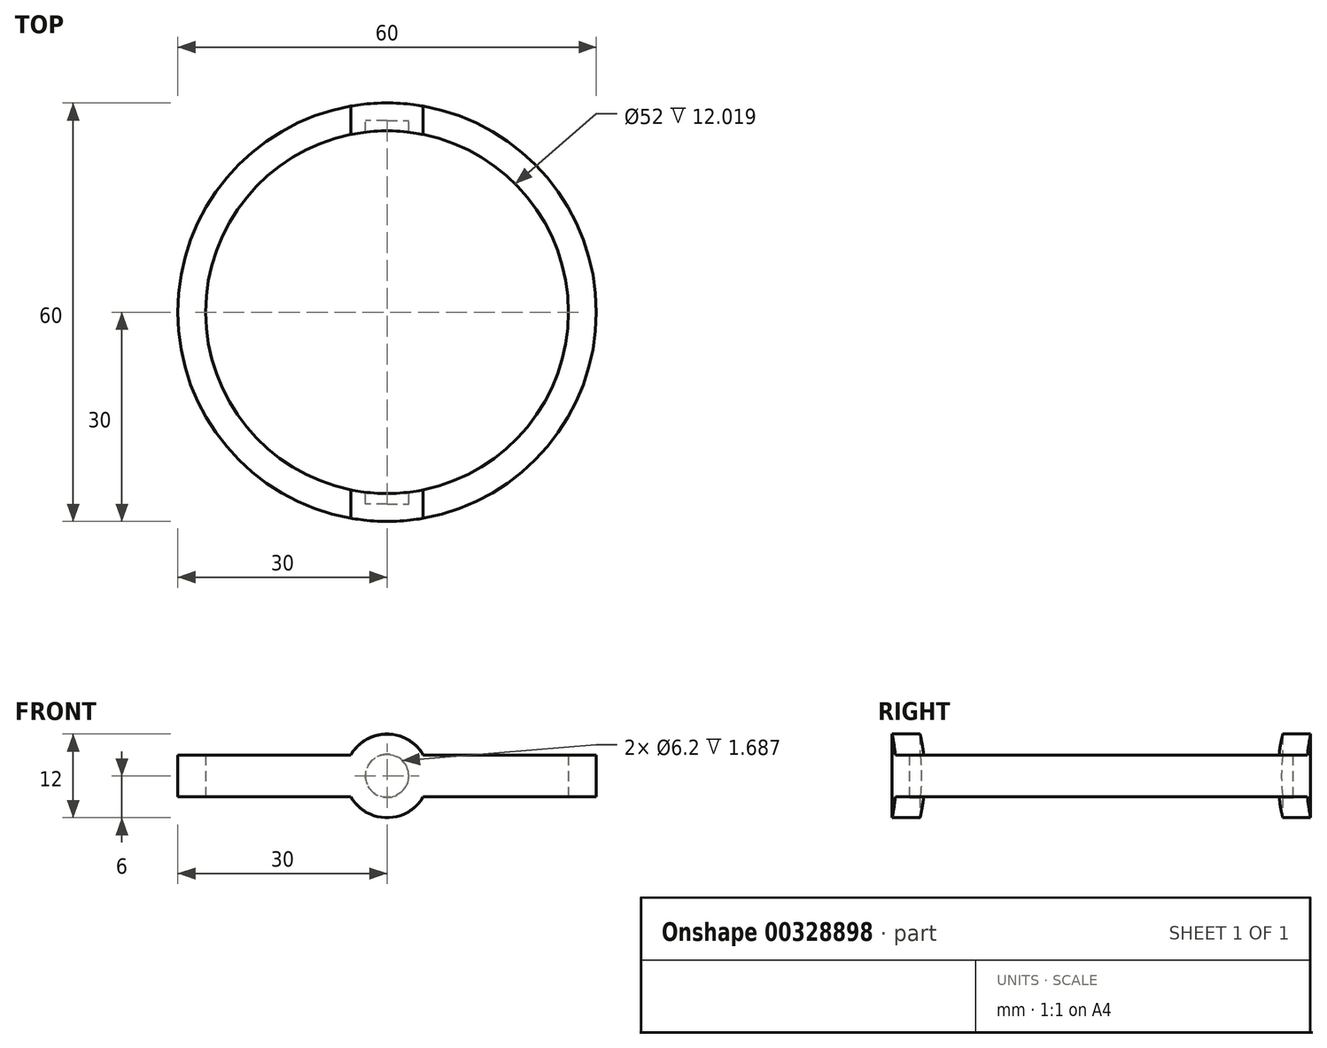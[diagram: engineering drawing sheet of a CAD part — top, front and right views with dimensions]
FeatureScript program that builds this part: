
annotation { "Feature Type Name" : "Feature", "Feature Type Description" : "" }
export const myFeature = defineFeature(function(context is Context, id is Id, definition is map)
    precondition{}
    {
        {
            var Q0;
            Q0=qCreatedBy(makeId("Front.planeOp"),FACE);
            var sketch = newSketch(context, id + "F0", { "sketchPlane" : qUnion([Q0])});
            skCircle(sketch, "E0", {"center": v(0, 0) * mm, "radius": 3 * mm, "construction": true});
            skCircle(sketch, "E1", {"center": v(0, 0) * mm, "radius": 1.5 * mm, "construction": true});
            skCircle(sketch, "E2", {"center": v(0, 0) * mm, "radius": 6 * mm});
            skLineSegment(sketch, "E3", {"start": v(2.65, 1.4) * mm, "end": v(5.3, 2.8) * mm, "construction": true});
            skLineSegment(sketch, "E4.bottom", {"start": v(0, -3) * mm, "end": v(-26, -3) * mm, "construction": true});
            skLineSegment(sketch, "E4.top", {"start": v(0, 3) * mm, "end": v(-26, 3) * mm, "construction": true});
            skLineSegment(sketch, "E4.left", {"start": v(0, -3) * mm, "end": v(0, 3) * mm});
            skLineSegment(sketch, "E4.right", {"start": v(-30, -3) * mm, "end": v(-30, 3) * mm});
            skLineSegment(sketch, "E5", {"start": v(-26, 3) * mm, "end": v(-26, -3) * mm});
            skLineSegment(sketch, "E6", {"start": v(-26, 3) * mm, "end": v(-26, 6) * mm});
            skLineSegment(sketch, "E7", {"start": v(-26, 6) * mm, "end": v(0, 6) * mm});
            skLineSegment(sketch, "E8", {"start": v(-26, -3) * mm, "end": v(-26, -6) * mm});
            skLineSegment(sketch, "E9", {"start": v(-26, -6) * mm, "end": v(0, -6) * mm});
            skLineSegment(sketch, "E10", {"start": v(0, 3) * mm, "end": v(0, 6) * mm});
            skLineSegment(sketch, "E11", {"start": v(0, -3) * mm, "end": v(0, -6) * mm});
            skLineSegment(sketch, "E12", {"start": v(-26, 3) * mm, "end": v(-30, 3) * mm});
            skLineSegment(sketch, "E13", {"start": v(-26, -3) * mm, "end": v(-30, -3) * mm});
            skSolve(sketch);
        }
        {
            var Q0;
            Q0=qCreatedBy(makeId("Front.planeOp"),FACE);
            var sketch = newSketch(context, id + "F1", { "sketchPlane" : qUnion([Q0])});
            skCircle(sketch, "E14.0", {"center": v(0, 0) * mm, "radius": 3 * mm, "construction": true});
            skCircle(sketch, "E15.0", {"center": v(0, 0) * mm, "radius": 1.5 * mm, "construction": true});
            skCircle(sketch, "E16.0", {"center": v(0, 0) * mm, "radius": 3.1 * mm});
            skCircle(sketch, "E17.0", {"center": v(0, 0) * mm, "radius": 1.55 * mm});
            skSolve(sketch);
        }
        {
            var Q0;
            {var subQ0=sQuery(id+"F0.wireOp",EDGE,"E4.right");Q0=makeQuery(id+"F0.imprint","IMPRINT",FACE,{"disambiguationData":[TD([[makeQuery(id+"F0.imprint","IMPRINT",EDGE,{"derivedFrom":subQ0}),-1.0]])]});}
            var Q1;
            Q1=sQuery(id+"F0.wireOp",EDGE,"E4.left");
            revolve(context, id + "F2", {"entities" : qUnion([Q0]), "axis" : qUnion([Q1]), "revolveType" : RevolveType.FULL});
        }
        {
            var Q0;
            Q0=makeQuery(id+"F0.imprint","IMPRINT",FACE,{"disambiguationData":[TD([[makeQuery(id+"F0.imprint","IMPRINT",EDGE,{"derivedFrom":sQuery(id+"F0.wireOp",EDGE,"E4.left")}),1.0]])]});
            var Q1;
            Q1=makeQuery(id+"F0.imprint","IMPRINT",FACE,{"disambiguationData":[TD([[makeQuery(id+"F0.imprint","IMPRINT",EDGE,{"derivedFrom":sQuery(id+"F0.wireOp",EDGE,"E4.left")}),-1.0]])]});
            var Q2;
            Q2=makeQuery(id+"F2.opRevolve","SWEPT_FACE",FACE,{"disambiguationData":[OSD([sQuery(id+"F0.wireOp",EDGE,"E4.right")])]});
            var Q3;
            Q3=makeQuery(id+"F2.opRevolve","SWEPT_FACE",FACE,{"disambiguationData":[OSD([sQuery(id+"F0.wireOp",EDGE,"E4.right")])]});
            extrude(context, id + "F3", {"entities" : qUnion([Q0, Q1]), "operationType" : NewBodyOperationType.ADD, "endBound" : BoundingType.UP_TO_SURFACE, "endBoundEntityFace" : qUnion([Q2]), "depth" : 35 * mm, "hasSecondDirection" : true, "secondDirectionBound" : SecondDirectionBoundingType.UP_TO_SURFACE, "secondDirectionOppositeDirection" : true, "secondDirectionBoundEntityFace" : qUnion([Q3]), "secondDirectionDepth" : 35 * mm});
        }
        {
            var Q0;
            Q0=makeQuery(id+"F0.imprint","IMPRINT",FACE,{"disambiguationData":[TD([[makeQuery(id+"F0.imprint","IMPRINT",EDGE,{"derivedFrom":sQuery(id+"F0.wireOp",EDGE,"E5")}),1.0]])]});
            var Q1;
            Q1=makeQuery(id+"F0.imprint","IMPRINT",FACE,{"disambiguationData":[TD([[makeQuery(id+"F0.imprint","IMPRINT",EDGE,{"derivedFrom":sQuery(id+"F0.wireOp",EDGE,"E4.left")}),1.0]])]});
            var Q2;
            Q2=sQuery(id+"F0.wireOp",EDGE,"E4.left");
            revolve(context, id + "F4", {"operationType" : NewBodyOperationType.REMOVE, "entities" : qUnion([Q0, Q1]), "axis" : qUnion([Q2]), "revolveType" : RevolveType.FULL, "oppositeDirection" : true});
        }
        {
            var Q0;
            Q0=makeQuery(id+"F1.imprint","IMPRINT",FACE,{"disambiguationData":[TD([[makeQuery(id+"F1.imprint","IMPRINT",EDGE,{"derivedFrom":sQuery(id+"F1.wireOp",EDGE,"E16.0")}),1.0]])]});
            var Q1;
            Q1=makeQuery(id+"F1.imprint","IMPRINT",FACE,{"disambiguationData":[TD([[makeQuery(id+"F1.imprint","IMPRINT",EDGE,{"derivedFrom":sQuery(id+"F1.wireOp",EDGE,"E17.0")}),1.0]])]});
            extrude(context, id + "F5", {"entities" : qUnion([Q0, Q1]), "operationType" : NewBodyOperationType.REMOVE, "endBound" : BoundingType.SYMMETRIC, "depth" : (30 * 2 - 2.5 * 2) * mm});
        }
    });
